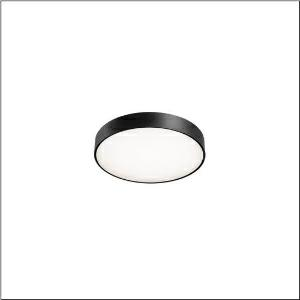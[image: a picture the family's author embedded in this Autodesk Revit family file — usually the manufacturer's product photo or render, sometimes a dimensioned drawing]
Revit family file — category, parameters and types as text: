
# Revit family: round_21_s_51mr34gd0421b
name_source: partatom
category: Lighting Fixtures
units: mm (PartAtom-declared; Revit-internal decimal feet)

## family parameters
Cut with Voids When Loaded = No
Host = Face
Light Source = No
Part Type = Normal
Room Calculation Point = No
Round Connector Dimension = Use Diameter
Shared = No

## types (1)
- Round 21 S (1 x LED, 3490 lm, 28 W, 4000K)
    Apparent Load = 28 VA
    CIE Flux Codes = 49 80 96 79 100
    Color Rendering = 80
    Color Temperature = 4000K
    Default Elevation = 1800 mm
    Description = Round 21 S, wall and ceiling luminaire, primary optical cover: cover, of PMMA, opal, light emission: direct/indirect distribution, primary light characteristic: symmetric, installation type: suspended mounting, surface-mounted, LED, rated luminous flux: 3.580lm, luminous efficacy: 118lm/W, light colour: 840, colour temperature: 4000K, with terminal, 5-pole, mains connection: 230V, AC, 50/60Hz, rated input power: 30W, housing, of aluminium, coated, black, diameter: 400mm, height: 62mm, protection rating (complete): IP40, insulation class (complete): insulation class I (protective earthing), certification: CE, impact resistance: IK04, permissible operating ambient temperature: -10..+35°C, packaging unit: 1 piece
    Height = 87 mm
    Lamp = 1 x LED
    Lamp Light Flux = 3490 lm
    Lamp Power = 28 W
    Lamp count = 1
    Length = 400 mm
    Luminous efficacy = 125 lm/W
    Manufacturer = Siteco
    ModVariant = No
    Model = 51MR34GD0421B
    Mounting Place = Ceiling
    Mounting Type = Surface mounted
    Number of Poles = 1
    OnlyDefault = Yes
    Power Factor = 1
    Product Name = Round 21 S
    Product group = wall and ceiling luminaire
    ProductGroupID = 301
    Protection Class = Protection class I
    Protection Degree = IP 40
    RLX_Detail_Level = 1
    RLX_Emergency_Light_Flux = 0 lm
    RLX_Emergency_Type = 0
    RLX_Emergency_Type_DB = No
    RlxData = <blob elided: 13833 chars, md5=df844139>
    Socket = socket
    Standby Power = 0 W
    System Light Flux = 3490 lm
    System Power = 28 W
    Type Comments = Product without accessories
    Type Image = l_1258311.jpg
    URL = http://relux.com
    VarID = ---
    Voltage = 0 V
    Weight = 0.00 kg
    Width = 0 mm  [stored 0 ft]

note: [stored X ft] marks values corroborated as IEEE doubles in the binary element streams (Revit-internal decimal feet)

## geometry (parser evidence)
native form markers: Sweep x11
no freeform markers — native parametric forms only
